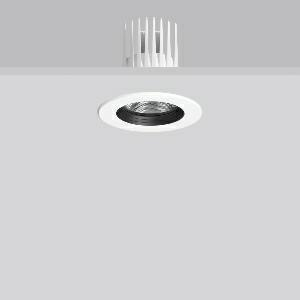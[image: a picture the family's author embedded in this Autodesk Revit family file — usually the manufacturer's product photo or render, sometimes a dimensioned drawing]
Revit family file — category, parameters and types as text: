
# Revit family: heledon_mini_e_901740_002_3_7806
name_source: partatom
category: Lighting Fixtures
units: mm (PartAtom-declared; Revit-internal decimal feet)

## family parameters
Cut with Voids When Loaded = No
Host = Face
Light Source = No
Part Type = Normal
Room Calculation Point = No
Round Connector Dimension = Use Diameter
Shared = No

## types (1)
- HELEDON mini E (1 x LED Modul 935, 2600 lm, 3500)
    Apparent Load = 20 VA
    Approval mark = CE
    CIE Flux Codes = 100 100 100 100 100
    Color Rendering = 92
    Color Temperature = 3500
    Default Elevation = 1800 mm
    Description = Series: HELEDON mini
Round recessed downlight. Housing: die-cast aluminium, powder-coated. Black plastic ring and recessed LED to prevent glare from the side. Optical assembly with reflector made of MIRO-Silver with 98% total light reflection for outstanding efficiency - can be changed without tools. Best colour rendering index Ra>90. Suitable for Recessed ceiling mounting. Installation without tools thanks to spring fastening system. Including separate LED converter with connecting cable 600 mm.High quality converter without flickering and stroboscopic effect. Through-wiring box (5 pole) available as accessory. The following accessories can be mounted without use of tools: interchangeable lenses, decorative glasses, honeycomb louvre, clear and frosted diffusers, white interchangeable plastic ring. 
Colour: traffic white, matt (RAL 9016)
Diameter: 124 mm
Height: 3 mm
Cut-out diameter: 114 mm
Recess height: 170 mm
Luminaire: recess height: 120 mm
Lamp: LED
Socket: without socket
Colour temperature: 3500K
Colour rendering index (CRI): 92
System power: 20 W
Rated luminous flux: 2600 lm
Luminous efficiency: 130 lm/W
Control gear: Regulated power supply
Protection class: II
Type of protection: IP 20
    Height = 0 mm  [stored 0 ft]
    Lamp = 1 x LED Modul 935
    Lamp Light Flux = 2600 lm
    Lamp count = 1
    Length = 124 mm  [stored 0.406824 ft]
    Lifetime = 50000 h
    Luminous efficacy = 130 lm/W
    Manufacturer = RZB
    ModVariant = No
    Model = 901740.002.3
    Mounting Place = Ceiling
    Mounting Type = Recessed
    Number of Poles = 1
    OnlyDefault = Yes
    Power Factor = 1
    Product Name = HELEDON mini E
    Product group = Recessed downlights
    ProductGroupID = 402
    Protection Class = Protection class II
    Protection Degree = IP 20
    RLX_Detail_Level = 1
    RLX_Emergency_Light_Flux = 0 lm
    RLX_Emergency_Type = 0
    RLX_Emergency_Type_DB = No
    RlxData = <blob elided: 125425 chars, md5=0735d347>
    Socket = socket
    Standby Power = 0 W
    System Light Flux = 2600 lm
    System Power = 20 W
    Type Comments = Product without accessories
    Type Image = 901657.002.jpg
    URL = http://relux.com
    VarID = ---
    Voltage = 230 V
    Voltage Range = 220-240 V
    Weight = 0.00 kg
    Width = 0 mm  [stored 0 ft]

note: [stored X ft] marks values corroborated as IEEE doubles in the binary element streams (Revit-internal decimal feet)

## geometry (parser evidence)
native form markers: Blend x4, Sweep x11
no freeform markers — native parametric forms only
